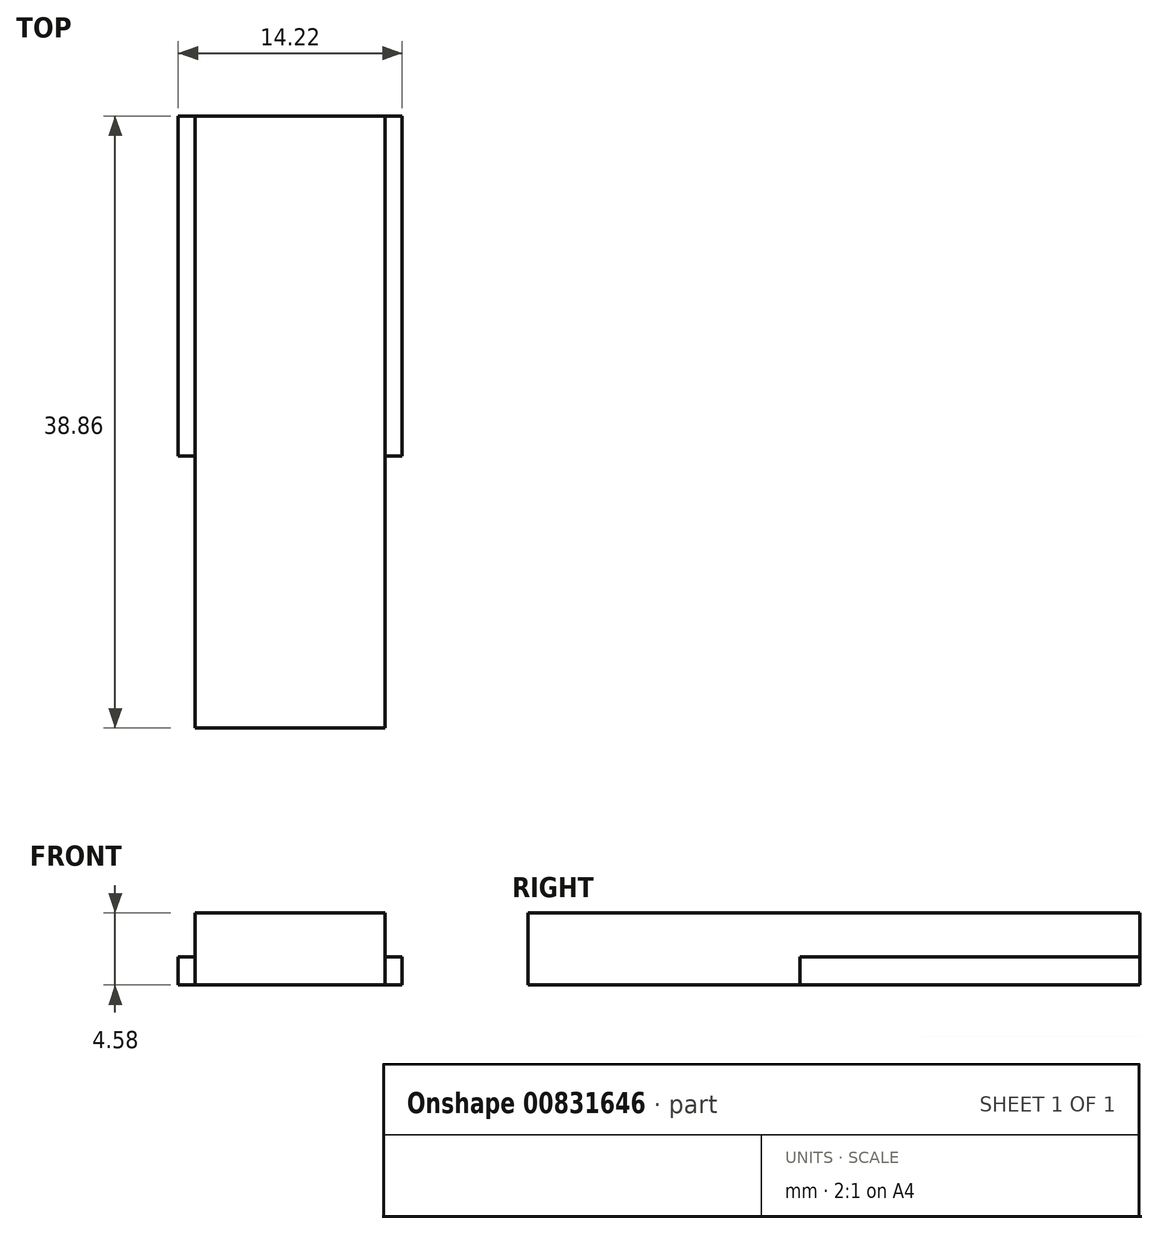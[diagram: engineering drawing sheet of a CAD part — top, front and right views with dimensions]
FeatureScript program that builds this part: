
annotation { "Feature Type Name" : "Feature", "Feature Type Description" : "" }
export const myFeature = defineFeature(function(context is Context, id is Id, definition is map)
    precondition{}
    {
        {
            var Q0;
            Q0=qCreatedBy(makeId("Front.planeOp"),FACE);
            var sketch = newSketch(context, id + "F0", { "sketchPlane" : qUnion([Q0])});
            skLineSegment(sketch, "E0.bottom", {"start": v(6.03, 2.29) * mm, "end": v(-6.03, 2.29) * mm});
            skLineSegment(sketch, "E0.top", {"start": v(6.03, -2.29) * mm, "end": v(-6.03, -2.29) * mm});
            skLineSegment(sketch, "E0.left", {"start": v(6.03, 2.29) * mm, "end": v(6.03, -2.29) * mm});
            skLineSegment(sketch, "E0.right", {"start": v(-6.03, 2.29) * mm, "end": v(-6.03, -2.29) * mm});
            skPoint(sketch, "E0.middle", {"position": v(0, 0) * mm});
            skSolve(sketch);
        }
        {
            var Q0;
            Q0 = qSketchRegion(id + "F0", true);
            extrude(context, id + "F1", {"entities" : qUnion([Q0]), "depth" : 17.27 * mm, "offsetDistance" : 25.4 * mm});
        }
        {
            var Q0;
            Q0=makeQuery(id+"F1.opExtrude","CAP_FACE",FACE,{"disambiguationData":[OSD([sQuery(id+"F0.wireOp",EDGE,"E0.bottom"),sQuery(id+"F0.wireOp",EDGE,"E0.top"),sQuery(id+"F0.wireOp",EDGE,"E0.left"),sQuery(id+"F0.wireOp",EDGE,"E0.right")])],"isStart":true});
            var sketch = newSketch(context, id + "F2", { "sketchPlane" : qUnion([Q0])});
            skLineSegment(sketch, "E1.bottom", {"start": v(6.03, 2.29) * mm, "end": v(-6.03, 2.29) * mm});
            skLineSegment(sketch, "E1.top", {"start": v(6.03, -2.29) * mm, "end": v(-6.03, -2.29) * mm});
            skLineSegment(sketch, "E1.left", {"start": v(6.03, 2.29) * mm, "end": v(6.03, -2.29) * mm});
            skLineSegment(sketch, "E1.right", {"start": v(-6.03, 2.29) * mm, "end": v(-6.03, -2.29) * mm});
            skPoint(sketch, "E1.middle", {"position": v(0, 0) * mm});
            skLineSegment(sketch, "E2.bottom", {"start": v(-7.11, -2.29) * mm, "end": v(7.11, -2.29) * mm});
            skLineSegment(sketch, "E2.top", {"start": v(-7.11, -0.5) * mm, "end": v(7.11, -0.5) * mm});
            skLineSegment(sketch, "E2.left", {"start": v(-7.11, -2.29) * mm, "end": v(-7.11, -0.5) * mm});
            skLineSegment(sketch, "E2.right", {"start": v(7.11, -2.29) * mm, "end": v(7.11, -0.5) * mm});
            skSolve(sketch);
        }
        {
            var Q0;
            Q0 = qSketchRegion(id + "F2", true);
            extrude(context, id + "F3", {"entities" : qUnion([Q0]), "operationType" : NewBodyOperationType.ADD, "depth" : 21.59 * mm, "offsetDistance" : 25.4 * mm});
        }
    });
